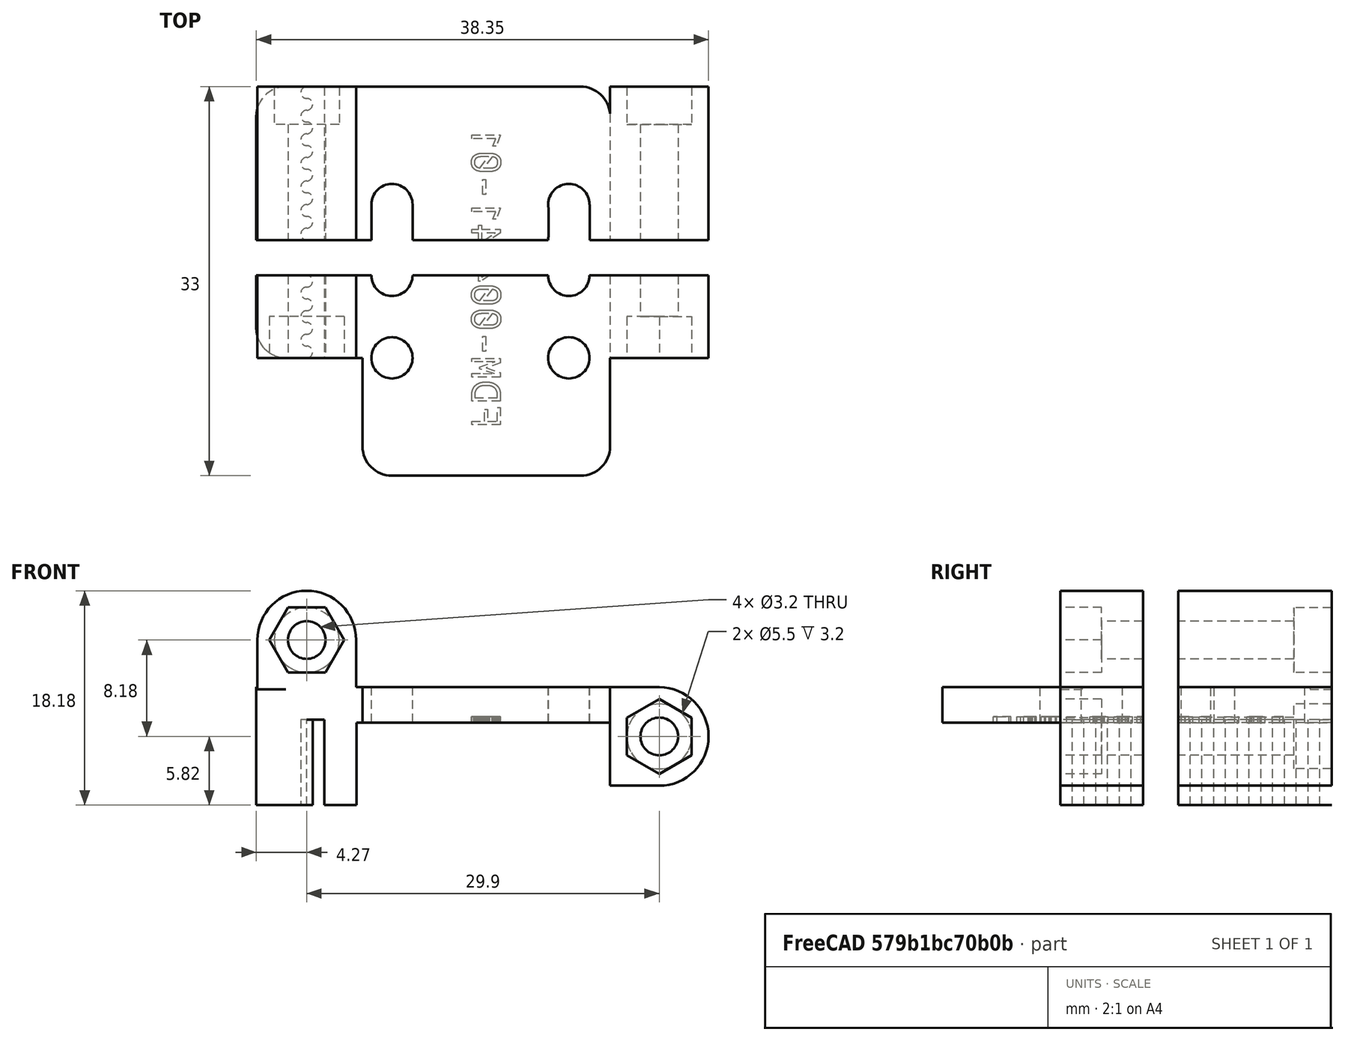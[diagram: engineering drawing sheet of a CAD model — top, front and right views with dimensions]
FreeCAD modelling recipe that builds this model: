
FCSTD DOCUMENT  (FreeCAD 0.19R24366 (Git))
Label: FDM-0041_modified
License: All rights reserved
LicenseURL: http://en.wikipedia.org/wiki/All_rights_reserved
objects: Part::Cylinder×8, Part::Box×6, Part::MultiFuse×6, Part::Cut×5, Part::RegularPolygon×2, Part::Extrusion×2, Part::Feature×2
note: 31 computed .brp shape members not serialized (recipe doc carries the construction recipe); baked Part::Feature solids carry a one-line shape summary decoded from their .brp

FEATURE [Part::Box] Box  label="Cube"
  AttacherType = Attacher::AttachEngine3D
  Height = 20
  Length = 40
  Placement = pos=(-38,15,-8) rot=(0,0,1;0rad)
  Width = 20
FEATURE [Part::Cylinder] Cylinder
  Angle = 360
  AttacherType = Attacher::AttachEngine3D
  Height = 20
  Placement = pos=(-33,48,7) rot=(1,0,0;1.5708rad)
  Radius = 4.18
FEATURE [Part::RegularPolygon] RegularPolygon  label="Regular polygon"
  AttacherType = Attacher::AttachEngine3D
  Circumradius = 3.18
  Polygon = 6
FEATURE [Part::Extrusion] Extrude
  Base = -> RegularPolygon
  Dir = (0,0,1)
  DirMode = 2
  FaceMakerClass = Part::FaceMakerBullseye
  LengthFwd = 3.5
  LengthRev = 0
  Placement = pos=(-33,31.5,7) rot=(1,0,0;1.5708rad)
  Solid = true
  Symmetric = false
FEATURE [Part::Cylinder] Cylinder001
  Angle = 360
  AttacherType = Attacher::AttachEngine3D
  Height = 20
  Placement = pos=(-33,48,7) rot=(1,0,0;1.5708rad)
  Radius = 1.6
FEATURE [Part::Cylinder] Cylinder002
  Angle = 360
  AttacherType = Attacher::AttachEngine3D
  Height = 3.2
  Placement = pos=(-33,48,7) rot=(1,0,0;1.5708rad)
  Radius = 2.75
FEATURE [Part::MultiFuse] Fusion  label="removes"
  Shapes = -> [Extrude,Cylinder001,Cylinder002]
FEATURE [Part::Box] Box002  label="Cube002"
  AttacherType = Attacher::AttachEngine3D
  Height = 4.18
  Length = 8.36
  Placement = pos=(-37.18,28,2.82) rot=(0,0,1;0rad)
  Width = 20
FEATURE [Part::MultiFuse] Fusion001  label="block"
  Shapes = -> [Cylinder,Box002]
FEATURE [Part::Cut] Cut
  Base = -> Fusion001
  Tool = -> Fusion
FEATURE [Part::Cylinder] Cylinder003
  Angle = 360
  AttacherType = Attacher::AttachEngine3D
  Height = 20
  Placement = pos=(-33,48,7) rot=(1,0,0;1.5708rad)
  Radius = 4.18
FEATURE [Part::Box] Box003  label="Cube003"
  AttacherType = Attacher::AttachEngine3D
  Height = 4.18
  Length = 8.36
  Placement = pos=(-37.18,28,2.82) rot=(0,0,1;0rad)
  Width = 20
FEATURE [Part::Cylinder] Cylinder004
  Angle = 360
  AttacherType = Attacher::AttachEngine3D
  Height = 3.2
  Placement = pos=(-33,48,7) rot=(1,0,0;1.5708rad)
  Radius = 2.75
FEATURE [Part::MultiFuse] Fusion003  label="block001"
  Shapes = -> [Cylinder003,Box003]
FEATURE [Part::Cylinder] Cylinder005
  Angle = 360
  AttacherType = Attacher::AttachEngine3D
  Height = 20
  Placement = pos=(-33,48,7) rot=(1,0,0;1.5708rad)
  Radius = 1.6
FEATURE [Part::RegularPolygon] RegularPolygon001  label="Regular polygon001"
  AttacherType = Attacher::AttachEngine3D
  Circumradius = 3.18
  Polygon = 6
FEATURE [Part::Extrusion] Extrude001
  Base = -> RegularPolygon001
  Dir = (0,0,1)
  DirMode = 2
  FaceMakerClass = Part::FaceMakerBullseye
  LengthFwd = 3.5
  LengthRev = 0
  Placement = pos=(-33,31.5,7) rot=(1,0,0;1.5708rad)
  Solid = true
  Symmetric = false
FEATURE [Part::MultiFuse] Fusion002  label="removes001"
  Shapes = -> [Extrude001,Cylinder005,Cylinder004]
FEATURE [Part::Cut] Cut001
  Base = -> Fusion003
  Placement = pos=(-10.1,0,-34.18) rot=(0,1,0;1.5708rad)
  Tool = -> Fusion002
FEATURE [Part::Cylinder] Cylinder006
  Angle = 360
  AttacherType = Attacher::AttachEngine3D
  Height = 10
  Placement = pos=(-25.77,35,-3) rot=(0,0,1;0rad)
  Radius = 1.75
FEATURE [Part::Cylinder] Cylinder007
  Angle = 360
  AttacherType = Attacher::AttachEngine3D
  Height = 10
  Placement = pos=(-10.77,35,-3) rot=(0,0,1;0rad)
  Radius = 1.75
FEATURE [Part::Box] Box004  label="Cube004"
  AttacherType = Attacher::AttachEngine3D
  Height = 4
  Length = 3.5
  Placement = pos=(-27.5,35,0) rot=(0,0,1;0rad)
  Width = 3
FEATURE [Part::Box] Box005  label="Cube005"
  AttacherType = Attacher::AttachEngine3D
  Height = 4
  Length = 3.5
  Placement = pos=(-12.5,35,0) rot=(0,0,1;0rad)
  Width = 3
FEATURE [Part::Feature] Part__Mirroring001  label="Body001"
  shape: bbox 30 x 30 x 10 mm, 281 faces (baked)
FEATURE [Part::MultiFuse] Fusion006
  Shapes = -> [Part__Mirroring001,Cut001,Cut]
FEATURE [Part::Box] Box001  label="Cube001"
  AttacherType = Attacher::AttachEngine3D
  Height = 20
  Length = 40
  Placement = pos=(-38,35,-8) rot=(0,0,1;0rad)
  Width = 21
FEATURE [Part::MultiFuse] Fusion007
  Shapes = -> [Cylinder006,Cylinder007,Box004,Box005]
FEATURE [Part::Cut] Cut002
  Base = -> Fusion006
  Tool = -> Fusion007
FEATURE [Part::Feature] Cut002001
  shape: bbox 38.35 x 30 x 18.18 mm, 347 faces (baked)
FEATURE [Part::Cut] Cut002002
  Base = -> Cut002
  Placement = pos=(0,-3,0) rot=(0,0,1;0rad)
  Tool = -> Box001
FEATURE [Part::Cut] Cut002003
  Base = -> Cut002001
  Tool = -> Box
